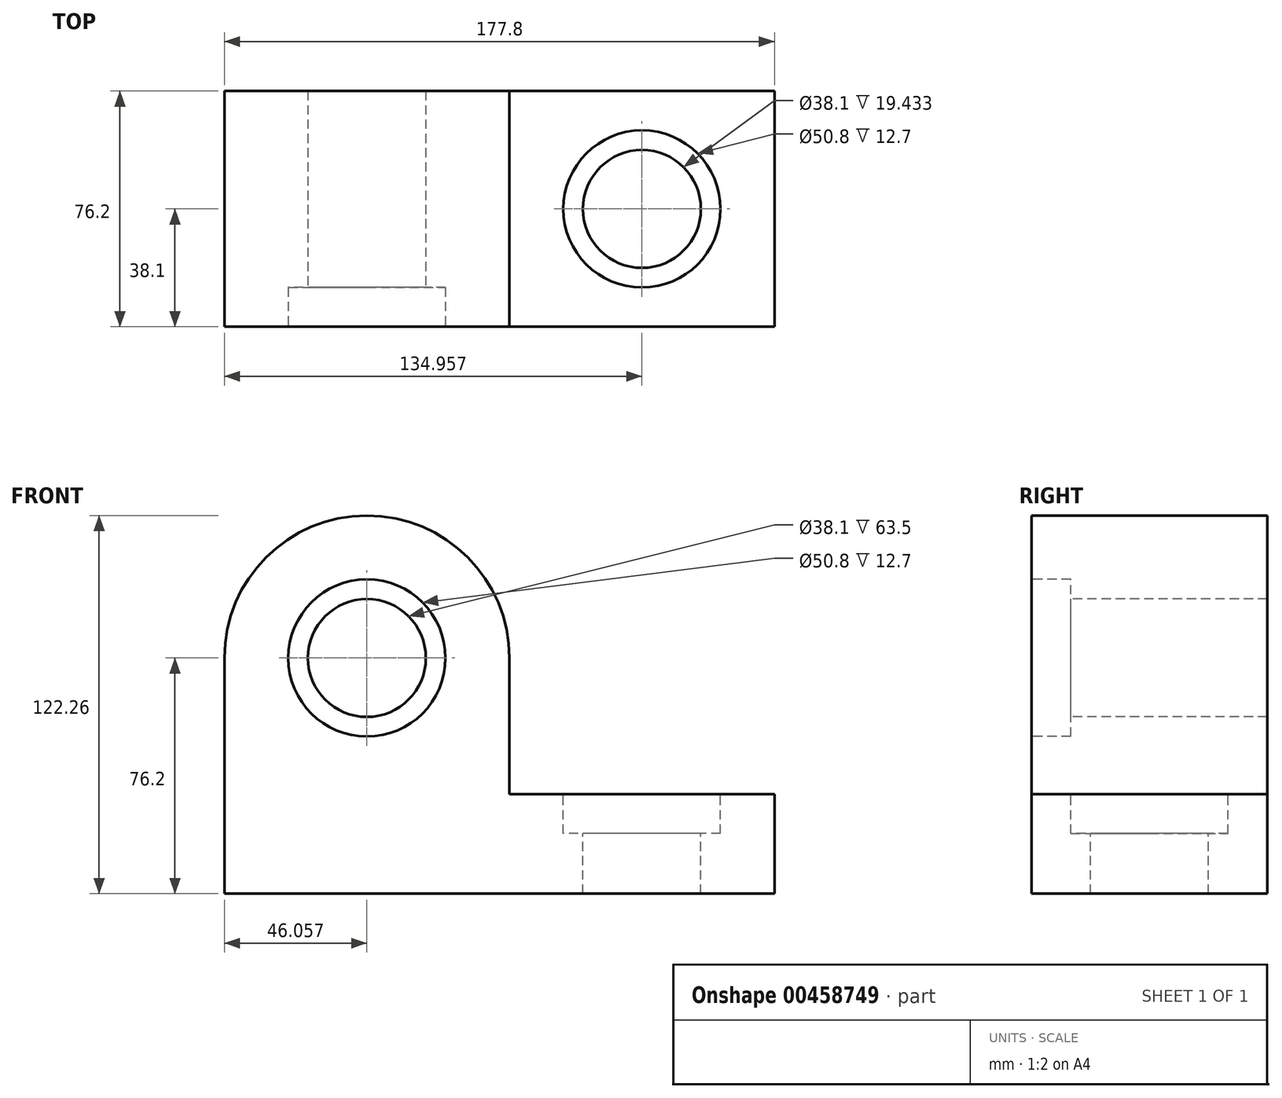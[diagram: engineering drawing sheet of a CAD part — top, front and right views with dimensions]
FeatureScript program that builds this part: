
annotation { "Feature Type Name" : "Feature", "Feature Type Description" : "" }
export const myFeature = defineFeature(function(context is Context, id is Id, definition is map)
    precondition{}
    {
        {
            var Q0;
            Q0=qCreatedBy(makeId("Front.planeOp"),FACE);
            var sketch = newSketch(context, id + "F0", { "sketchPlane" : qUnion([Q0])});
            skLineSegment(sketch, "E0", {"start": v(0, 0) * mm, "end": v(177.8, 0) * mm});
            skLineSegment(sketch, "E1", {"start": v(177.8, 0) * mm, "end": v(177.8, 32.13) * mm});
            skLineSegment(sketch, "E2", {"start": v(177.8, 32.13) * mm, "end": v(92.11, 32.13) * mm});
            skLineSegment(sketch, "E3", {"start": v(0, 0) * mm, "end": v(0, 76.2) * mm});
            skLineSegment(sketch, "E4", {"start": v(92.11, 32.13) * mm, "end": v(92.11, 76.2) * mm});
            skArc(sketch, "E5", {"start": v(92.11, 76.2) * mm, "mid": v(46.06, 122.26) * mm, "end": v(0, 76.2) * mm});
            skCircle(sketch, "E6", {"center": v(46.06, 76.2) * mm, "radius": 25.4 * mm});
            skCircle(sketch, "E7", {"center": v(46.06, 76.2) * mm, "radius": 19.05 * mm});
            skSolve(sketch);
        }
        {
            var Q0;
            Q0 = qSketchRegion(id + "F0", true);
            var Q1;
            Q1=makeQuery(id+"F0.imprint","IMPRINT",FACE,{"disambiguationData":[TD([[makeQuery(id+"F0.imprint","IMPRINT",EDGE,{"derivedFrom":sQuery(id+"F0.wireOp",EDGE,"E6")}),1.0]])]});
            extrude(context, id + "F1", {"entities" : qUnion([Q0, Q1]), "oppositeDirection" : true, "depth" : 76.2 * mm});
        }
        {
            var Q0;
            Q0=makeQuery(id+"F0.imprint","IMPRINT",FACE,{"disambiguationData":[TD([[makeQuery(id+"F0.imprint","IMPRINT",EDGE,{"derivedFrom":sQuery(id+"F0.wireOp",EDGE,"E6")}),1.0]])]});
            extrude(context, id + "F2", {"entities" : qUnion([Q0]), "operationType" : NewBodyOperationType.REMOVE, "oppositeDirection" : true, "depth" : 12.7 * mm});
        }
        {
            var Q0;
            Q0=makeQuery(id+"F1.opExtrude","SWEPT_FACE",FACE,{"disambiguationData":[OSD([sQuery(id+"F0.wireOp",EDGE,"E2")])]});
            var sketch = newSketch(context, id + "F3", { "sketchPlane" : qUnion([Q0])});
            skCircle(sketch, "E8", {"center": v(134.96, 38.1) * mm, "radius": 25.4 * mm});
            skCircle(sketch, "E9", {"center": v(134.96, 38.1) * mm, "radius": 19.05 * mm});
            skSolve(sketch);
        }
        {
            var Q0;
            Q0=makeQuery(id+"F3.imprint","IMPRINT",FACE,{"disambiguationData":[TD([[makeQuery(id+"F3.imprint","IMPRINT",EDGE,{"derivedFrom":sQuery(id+"F3.wireOp",EDGE,"E9")}),1.0]])]});
            extrude(context, id + "F4", {"entities" : qUnion([Q0]), "operationType" : NewBodyOperationType.REMOVE, "endBound" : BoundingType.THROUGH_ALL, "oppositeDirection" : true, "depth" : 25.4 * mm});
        }
        {
            var Q0;
            Q0=makeQuery(id+"F3.imprint","IMPRINT",FACE,{"disambiguationData":[TD([[makeQuery(id+"F3.imprint","IMPRINT",EDGE,{"derivedFrom":sQuery(id+"F3.wireOp",EDGE,"E8")}),1.0]])]});
            extrude(context, id + "F5", {"entities" : qUnion([Q0]), "operationType" : NewBodyOperationType.REMOVE, "oppositeDirection" : true, "depth" : 12.7 * mm});
        }
    });
